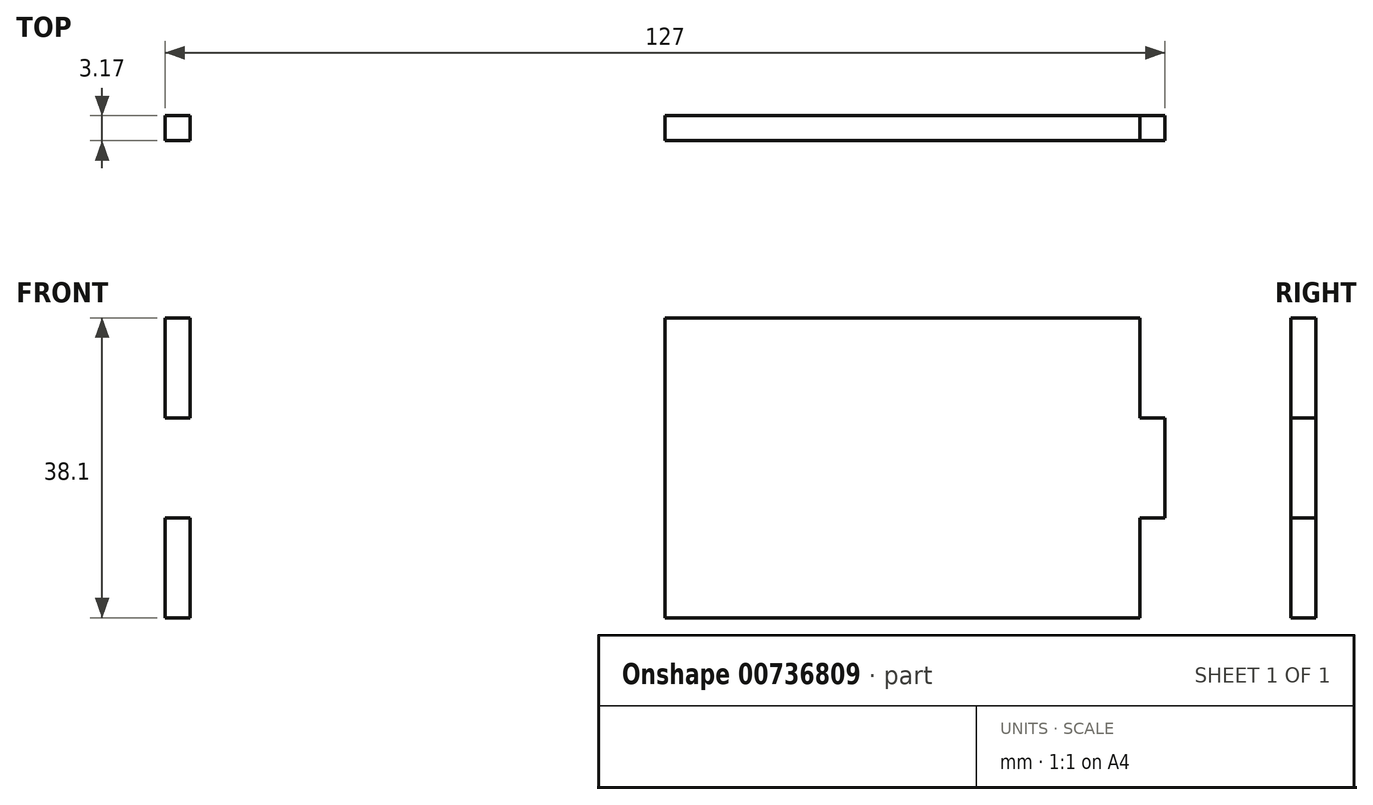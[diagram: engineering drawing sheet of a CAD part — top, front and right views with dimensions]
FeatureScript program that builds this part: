
annotation { "Feature Type Name" : "Feature", "Feature Type Description" : "" }
export const myFeature = defineFeature(function(context is Context, id is Id, definition is map)
    precondition{}
    {
        {
            var Q0;
            Q0=qCreatedBy(makeId("Front.planeOp"),FACE);
            var sketch = newSketch(context, id + "F0", { "sketchPlane" : qUnion([Q0])});
            skLineSegment(sketch, "E0.bottom", {"start": v(0, 0) * mm, "end": v(-127, 0) * mm});
            skLineSegment(sketch, "E0.top", {"start": v(0, 38.1) * mm, "end": v(-127, 38.1) * mm});
            skLineSegment(sketch, "E0.left", {"start": v(0, 0) * mm, "end": v(0, 38.1) * mm});
            skLineSegment(sketch, "E0.right", {"start": v(-127, 0) * mm, "end": v(-127, 38.1) * mm});
            skLineSegment(sketch, "E1.bottom", {"start": v(-127, 0) * mm, "end": v(-123.83, 0) * mm});
            skLineSegment(sketch, "E1.top", {"start": v(-127, 12.7) * mm, "end": v(-123.83, 12.7) * mm});
            skLineSegment(sketch, "E1.left", {"start": v(-127, 0) * mm, "end": v(-127, 12.7) * mm});
            skLineSegment(sketch, "E1.right", {"start": v(-123.83, 0) * mm, "end": v(-123.83, 12.7) * mm});
            skLineSegment(sketch, "E2.bottom", {"start": v(-127, 38.1) * mm, "end": v(-123.83, 38.1) * mm});
            skLineSegment(sketch, "E2.top", {"start": v(-127, 25.4) * mm, "end": v(-123.83, 25.4) * mm});
            skLineSegment(sketch, "E2.left", {"start": v(-127, 38.1) * mm, "end": v(-127, 25.4) * mm});
            skLineSegment(sketch, "E2.right", {"start": v(-123.83, 38.1) * mm, "end": v(-123.83, 25.4) * mm});
            skLineSegment(sketch, "E3", {"start": v(-63.5, 0) * mm, "end": v(-63.5, 38.1) * mm});
            skLineSegment(sketch, "E4.MirrorCS", {"start": v(-3.18, 38.1) * mm, "end": v(-3.18, 25.4) * mm});
            skLineSegment(sketch, "E5.MirrorCS", {"start": v(0, 25.4) * mm, "end": v(-3.18, 25.4) * mm});
            skLineSegment(sketch, "E6.MirrorCS", {"start": v(0, 12.7) * mm, "end": v(-3.17, 12.7) * mm});
            skLineSegment(sketch, "E7.MirrorCS", {"start": v(-3.17, 0) * mm, "end": v(-3.17, 12.7) * mm});
            skSolve(sketch);
        }
        {
            var Q0;
            Q0=makeQuery(id+"F0.imprint","IMPRINT",FACE,{"disambiguationData":[TD([[makeQuery(id+"F0.imprint","IMPRINT",EDGE,{"derivedFrom":sQuery(id+"F0.wireOp",EDGE,"E0.right")}),-1.0]])]});
            var Q1;
            {var subQ0=sQuery(id+"F0.wireOp",EDGE,"E3");Q1=makeQuery(id+"F0.imprint","IMPRINT",FACE,{"disambiguationData":[TD([[makeQuery(id+"F0.imprint","IMPRINT",EDGE,{"derivedFrom":subQ0}),-1.0]])]});}
            extrude(context, id + "F1", {"entities" : qUnion([Q0, Q1]), "depth" : 3.17 * mm, "offsetDistance" : 25.4 * mm});
        }
        {
            var Q0;
            Q0=makeQuery(id+"F0.imprint","IMPRINT",FACE,{"disambiguationData":[TD([[makeQuery(id+"F0.imprint","IMPRINT",EDGE,{"derivedFrom":sQuery(id+"F0.wireOp",EDGE,"E1.bottom")}),1.0]])]});
            var Q1;
            Q1=makeQuery(id+"F0.imprint","IMPRINT",FACE,{"disambiguationData":[TD([[makeQuery(id+"F0.imprint","IMPRINT",EDGE,{"derivedFrom":sQuery(id+"F0.wireOp",EDGE,"E2.bottom")}),-1.0]])]});
            var Q2;
            {var subQ3=sQuery(id+"F0.wireOp",EDGE,"E4.MirrorCS");Q2=makeQuery(id+"F0.imprint","IMPRINT",FACE,{"disambiguationData":[TD([[makeQuery(id+"F0.imprint","IMPRINT",EDGE,{"derivedFrom":subQ3}),1.0]])]});}
            var Q3;
            {var subQ4=sQuery(id+"F0.wireOp",EDGE,"E6.MirrorCS");Q3=makeQuery(id+"F0.imprint","IMPRINT",FACE,{"disambiguationData":[TD([[makeQuery(id+"F0.imprint","IMPRINT",EDGE,{"derivedFrom":subQ4}),1.0]])]});}
            extrude(context, id + "F2", {"entities" : qUnion([Q0, Q1, Q2, Q3]), "operationType" : NewBodyOperationType.REMOVE, "oppositeDirection" : true, "depth" : 25.4 * mm, "offsetDistance" : 25.4 * mm});
        }
    });
